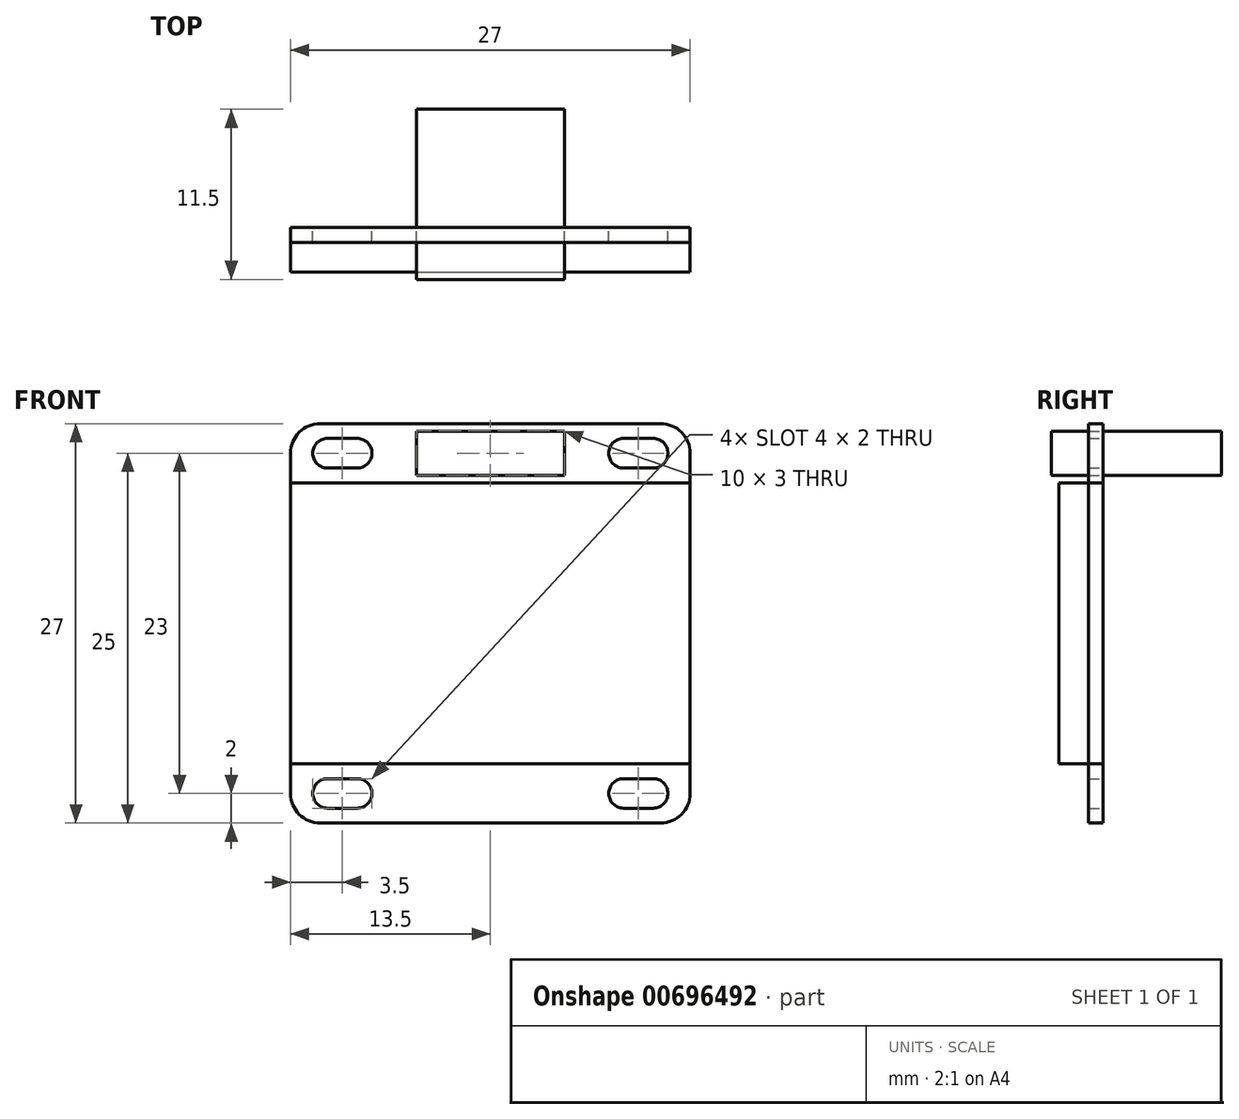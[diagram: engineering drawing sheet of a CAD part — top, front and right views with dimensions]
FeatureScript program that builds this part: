
annotation { "Feature Type Name" : "Feature", "Feature Type Description" : "" }
export const myFeature = defineFeature(function(context is Context, id is Id, definition is map)
    precondition{}
    {
        {
            var Q0;
            Q0=qCreatedBy(makeId("Front.planeOp"),FACE);
            var sketch = newSketch(context, id + "F0", { "sketchPlane" : qUnion([Q0])});
            skLineSegment(sketch, "E0.bottom", {"start": v(11.5, -13.5) * mm, "end": v(-11.5, -13.5) * mm});
            skLineSegment(sketch, "E0.top", {"start": v(11.5, 13.5) * mm, "end": v(-11.5, 13.5) * mm});
            skLineSegment(sketch, "E0.left", {"start": v(13.5, -11.5) * mm, "end": v(13.5, 11.5) * mm});
            skLineSegment(sketch, "E0.right", {"start": v(-13.5, -11.5) * mm, "end": v(-13.5, 11.5) * mm});
            skPoint(sketch, "E0.middle", {"position": v(0, 0) * mm});
            skPoint(sketch, "E1.visualSharp", {"position": v(-13.5, 13.5) * mm});
            skArc(sketch, "E1.filletArc", {"start": v(-11.5, 13.5) * mm, "mid": v(-12.91, 12.91) * mm, "end": v(-13.5, 11.5) * mm});
            skPoint(sketch, "E2.visualSharp", {"position": v(-13.5, -13.5) * mm});
            skArc(sketch, "E2.filletArc", {"start": v(-13.5, -11.5) * mm, "mid": v(-12.91, -12.91) * mm, "end": v(-11.5, -13.5) * mm});
            skPoint(sketch, "E3.visualSharp", {"position": v(13.5, -13.5) * mm});
            skArc(sketch, "E3.filletArc", {"start": v(11.5, -13.5) * mm, "mid": v(12.91, -12.91) * mm, "end": v(13.5, -11.5) * mm});
            skPoint(sketch, "E4.visualSharp", {"position": v(13.5, 13.5) * mm});
            skArc(sketch, "E4.filletArc", {"start": v(13.5, 11.5) * mm, "mid": v(12.91, 12.91) * mm, "end": v(11.5, 13.5) * mm});
            skLineSegment(sketch, "E5.bottom", {"start": v(-9, 10.5) * mm, "end": v(-11, 10.5) * mm});
            skLineSegment(sketch, "E5.top", {"start": v(-9, 12.5) * mm, "end": v(-11, 12.5) * mm});
            skLineSegment(sketch, "E5.left", {"start": v(-8, 11.5) * mm, "end": v(-8, 11.5) * mm});
            skLineSegment(sketch, "E5.right", {"start": v(-12, 11.5) * mm, "end": v(-12, 11.5) * mm});
            skLineSegment(sketch, "E6", {"start": v(-9.79, 12.5) * mm, "end": v(-9.79, 13.5) * mm, "construction": true});
            skLineSegment(sketch, "E7", {"start": v(-12, 10.76) * mm, "end": v(-13.5, 10.76) * mm, "construction": true});
            skPoint(sketch, "E8.visualSharp", {"position": v(-12, 12.5) * mm});
            skArc(sketch, "E8.filletArc", {"start": v(-11, 12.5) * mm, "mid": v(-11.7, 12.2) * mm, "end": v(-12, 11.5) * mm});
            skPoint(sketch, "E9.visualSharp", {"position": v(-12, 10.5) * mm});
            skArc(sketch, "E9.filletArc", {"start": v(-12, 11.5) * mm, "mid": v(-11.7, 10.8) * mm, "end": v(-11, 10.5) * mm});
            skPoint(sketch, "E10.visualSharp", {"position": v(-8, 10.5) * mm});
            skArc(sketch, "E10.filletArc", {"start": v(-9, 10.5) * mm, "mid": v(-8.3, 10.8) * mm, "end": v(-8, 11.5) * mm});
            skPoint(sketch, "E11.visualSharp", {"position": v(-8, 12.5) * mm});
            skArc(sketch, "E11.filletArc", {"start": v(-8, 11.5) * mm, "mid": v(-8.3, 12.2) * mm, "end": v(-9, 12.5) * mm});
            skArc(sketch, "E12.MirrorCS", {"start": v(8, 11.5) * mm, "mid": v(8.3, 12.2) * mm, "end": v(9, 12.5) * mm});
            skArc(sketch, "E13.MirrorCS", {"start": v(11, 12.5) * mm, "mid": v(11.7, 12.2) * mm, "end": v(12, 11.5) * mm});
            skLineSegment(sketch, "E14.MirrorCS", {"start": v(9.79, 12.5) * mm, "end": v(9.79, 13.5) * mm, "construction": true});
            skArc(sketch, "E15.MirrorCS", {"start": v(9, 10.5) * mm, "mid": v(8.3, 10.8) * mm, "end": v(8, 11.5) * mm});
            skArc(sketch, "E16.MirrorCS", {"start": v(12, 11.5) * mm, "mid": v(11.7, 10.8) * mm, "end": v(11, 10.5) * mm});
            skPoint(sketch, "E17.MirrorP", {"position": v(8, 12.5) * mm});
            skPoint(sketch, "E18.MirrorP", {"position": v(8, 10.5) * mm});
            skPoint(sketch, "E19.MirrorP", {"position": v(12, 12.5) * mm});
            skPoint(sketch, "E20.MirrorP", {"position": v(12, 10.5) * mm});
            skLineSegment(sketch, "E21.MirrorCS", {"start": v(12, 11.5) * mm, "end": v(12, 11.5) * mm});
            skLineSegment(sketch, "E22.MirrorCS", {"start": v(9, 10.5) * mm, "end": v(11, 10.5) * mm});
            skLineSegment(sketch, "E23.MirrorCS", {"start": v(8, 11.5) * mm, "end": v(8, 11.5) * mm});
            skLineSegment(sketch, "E24.MirrorCS", {"start": v(9, 12.5) * mm, "end": v(11, 12.5) * mm});
            skLineSegment(sketch, "E25.MirrorCS", {"start": v(12, 10.76) * mm, "end": v(13.5, 10.76) * mm, "construction": true});
            skArc(sketch, "E26.MirrorCS", {"start": v(-12, -11.5) * mm, "mid": v(-11.7, -10.8) * mm, "end": v(-11, -10.5) * mm});
            skArc(sketch, "E27.MirrorCS", {"start": v(-11, -12.5) * mm, "mid": v(-11.7, -12.2) * mm, "end": v(-12, -11.5) * mm});
            skLineSegment(sketch, "E28.MirrorCS", {"start": v(-9.79, -12.5) * mm, "end": v(-9.79, -13.5) * mm, "construction": true});
            skArc(sketch, "E29.MirrorCS", {"start": v(-8, -11.5) * mm, "mid": v(-8.3, -12.2) * mm, "end": v(-9, -12.5) * mm});
            skArc(sketch, "E30.MirrorCS", {"start": v(-9, -10.5) * mm, "mid": v(-8.3, -10.8) * mm, "end": v(-8, -11.5) * mm});
            skPoint(sketch, "E31.MirrorP", {"position": v(-12, -12.5) * mm});
            skLineSegment(sketch, "E32.MirrorCS", {"start": v(-8, -11.5) * mm, "end": v(-8, -11.5) * mm});
            skPoint(sketch, "E33.MirrorP", {"position": v(-12, -10.5) * mm});
            skPoint(sketch, "E34.MirrorP", {"position": v(-8, -10.5) * mm});
            skLineSegment(sketch, "E35.MirrorCS", {"start": v(-12, -11.5) * mm, "end": v(-12, -11.5) * mm});
            skLineSegment(sketch, "E36.MirrorCS", {"start": v(-12, -10.76) * mm, "end": v(-13.5, -10.76) * mm, "construction": true});
            skLineSegment(sketch, "E37.MirrorCS", {"start": v(-9, -12.5) * mm, "end": v(-11, -12.5) * mm});
            skLineSegment(sketch, "E38.MirrorCS", {"start": v(-9, -10.5) * mm, "end": v(-11, -10.5) * mm});
            skArc(sketch, "E39.MirrorCS", {"start": v(-11.5, -13.5) * mm, "mid": v(-12.91, -12.91) * mm, "end": v(-13.5, -11.5) * mm});
            skPoint(sketch, "E40.MirrorP", {"position": v(-8, -12.5) * mm});
            skArc(sketch, "E41.MirrorCS", {"start": v(11, -12.5) * mm, "mid": v(11.7, -12.2) * mm, "end": v(12, -11.5) * mm});
            skArc(sketch, "E42.MirrorCS", {"start": v(9, -10.5) * mm, "mid": v(8.3, -10.8) * mm, "end": v(8, -11.5) * mm});
            skArc(sketch, "E43.MirrorCS", {"start": v(8, -11.5) * mm, "mid": v(8.3, -12.2) * mm, "end": v(9, -12.5) * mm});
            skArc(sketch, "E44.MirrorCS", {"start": v(12, -11.5) * mm, "mid": v(11.7, -10.8) * mm, "end": v(11, -10.5) * mm});
            skPoint(sketch, "E45.MirrorP", {"position": v(12, -12.5) * mm});
            skLineSegment(sketch, "E46.MirrorCS", {"start": v(9, -12.5) * mm, "end": v(11, -12.5) * mm});
            skLineSegment(sketch, "E47.MirrorCS", {"start": v(12, -11.5) * mm, "end": v(12, -11.5) * mm});
            skPoint(sketch, "E48.MirrorP", {"position": v(8, -10.5) * mm});
            skPoint(sketch, "E49.MirrorP", {"position": v(12, -10.5) * mm});
            skLineSegment(sketch, "E50.MirrorCS", {"start": v(9, -10.5) * mm, "end": v(11, -10.5) * mm});
            skLineSegment(sketch, "E51.MirrorCS", {"start": v(8, -11.5) * mm, "end": v(8, -11.5) * mm});
            skPoint(sketch, "E52.MirrorP", {"position": v(8, -12.5) * mm});
            skLineSegment(sketch, "E53.bottom", {"start": v(-13.5, -9.5) * mm, "end": v(13.5, -9.5) * mm});
            skLineSegment(sketch, "E53.top", {"start": v(-13.5, 9.5) * mm, "end": v(13.5, 9.5) * mm});
            skLineSegment(sketch, "E53.left", {"start": v(-13.5, -9.5) * mm, "end": v(-13.5, 9.5) * mm});
            skLineSegment(sketch, "E53.right", {"start": v(13.5, -9.5) * mm, "end": v(13.5, 9.5) * mm});
            skLineSegment(sketch, "E54", {"start": v(-1.47, -13.5) * mm, "end": v(-1.47, -9.5) * mm, "construction": true});
            skLineSegment(sketch, "E55", {"start": v(-2.55, 9.5) * mm, "end": v(-2.55, 13.5) * mm, "construction": true});
            skLineSegment(sketch, "E56.bottom", {"start": v(5, 10) * mm, "end": v(-5, 10) * mm});
            skLineSegment(sketch, "E56.top", {"start": v(5, 13) * mm, "end": v(-5, 13) * mm});
            skLineSegment(sketch, "E56.left", {"start": v(5, 10) * mm, "end": v(5, 13) * mm});
            skLineSegment(sketch, "E56.right", {"start": v(-5, 10) * mm, "end": v(-5, 13) * mm});
            skPoint(sketch, "E56.middle", {"position": v(0, 11.5) * mm});
            skLineSegment(sketch, "E57", {"start": v(-4.03, 13) * mm, "end": v(-4.03, 13.5) * mm, "construction": true});
            skSolve(sketch);
        }
        {
            var Q0;
            Q0=makeQuery(id+"F0.imprint","IMPRINT",FACE,{"disambiguationData":[TD([[makeQuery(id+"F0.imprint","IMPRINT",EDGE,{"derivedFrom":sQuery(id+"F0.wireOp",EDGE,"E0.top")}),1.0]])]});
            var Q1;
            Q1=makeQuery(id+"F0.imprint","IMPRINT",FACE,{"disambiguationData":[TD([[makeQuery(id+"F0.imprint","IMPRINT",EDGE,{"derivedFrom":sQuery(id+"F0.wireOp",EDGE,"E53.bottom")}),1.0]])]});
            var Q2;
            Q2=makeQuery(id+"F0.imprint","IMPRINT",FACE,{"disambiguationData":[TD([[makeQuery(id+"F0.imprint","IMPRINT",EDGE,{"derivedFrom":sQuery(id+"F0.wireOp",EDGE,"E0.bottom")}),-1.0]])]});
            extrude(context, id + "F1", {"entities" : qUnion([Q0, Q1, Q2]), "depth" : 1 * mm, "offsetDistance" : 25 * mm});
        }
        {
            var Q0;
            Q0=makeQuery(id+"F0.imprint","IMPRINT",FACE,{"disambiguationData":[TD([[makeQuery(id+"F0.imprint","IMPRINT",EDGE,{"derivedFrom":sQuery(id+"F0.wireOp",EDGE,"E53.bottom")}),1.0]])]});
            extrude(context, id + "F2", {"entities" : qUnion([Q0]), "depth" : 3 * mm, "offsetDistance" : 25 * mm});
        }
        {
            var Q0;
            Q0=makeQuery(id+"F0.imprint","IMPRINT",FACE,{"disambiguationData":[TD([[makeQuery(id+"F0.imprint","IMPRINT",EDGE,{"derivedFrom":sQuery(id+"F0.wireOp",EDGE,"E56.bottom")}),-1.0]])]});
            extrude(context, id + "F3", {"entities" : qUnion([Q0]), "depth" : 3.5 * mm, "offsetDistance" : 25 * mm, "hasSecondDirection" : true, "secondDirectionOppositeDirection" : true, "secondDirectionDepth" : 8 * mm});
        }
    });
